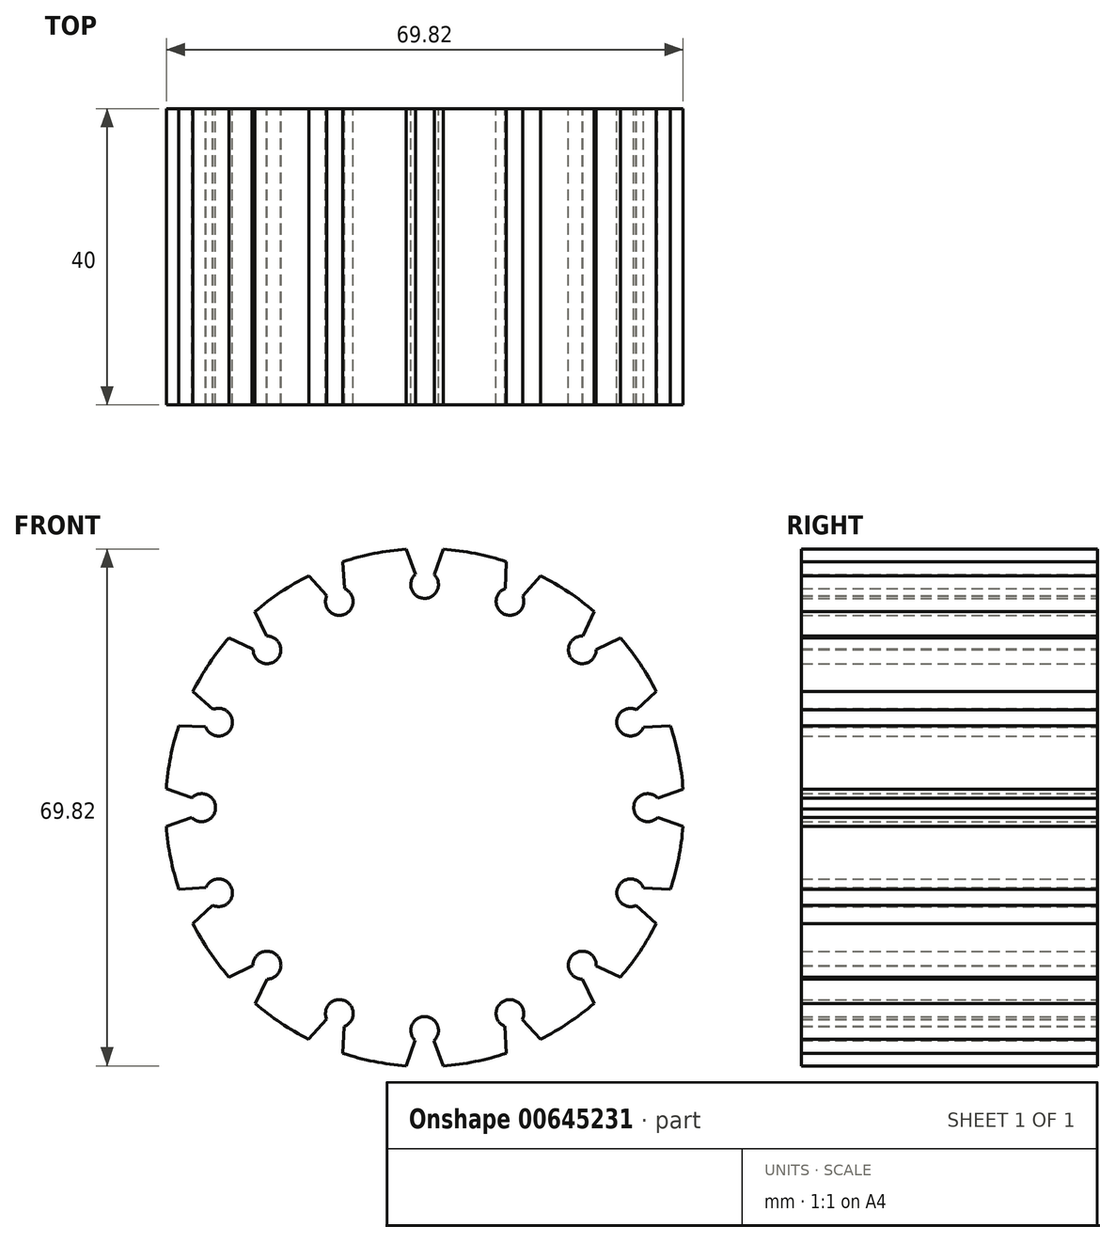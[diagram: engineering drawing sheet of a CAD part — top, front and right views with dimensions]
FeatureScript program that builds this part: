
annotation { "Feature Type Name" : "Feature", "Feature Type Description" : "" }
export const myFeature = defineFeature(function(context is Context, id is Id, definition is map)
    precondition{}
    {
        {
            var Q0;
            Q0=qCreatedBy(makeId("Front.planeOp"),FACE);
            var sketch = newSketch(context, id + "F0", { "sketchPlane" : qUnion([Q0])});
            skCircle(sketch, "E0", {"center": v(0, 0) * mm, "radius": 35 * mm});
            skLineSegment(sketch, "E1", {"start": v(0, -35) * mm, "end": v(0, 35) * mm, "construction": true});
            skLineSegment(sketch, "E2", {"start": v(35, 0) * mm, "end": v(-35, 0) * mm, "construction": true});
            skLineSegment(sketch, "E3", {"start": v(-24.75, -24.75) * mm, "end": v(24.75, 24.75) * mm, "construction": true});
            skLineSegment(sketch, "E4", {"start": v(-24.75, 24.75) * mm, "end": v(24.75, -24.75) * mm, "construction": true});
            skLineSegment(sketch, "E5.0", {"start": v(-2.5, 34.91) * mm, "end": v(2.5, 34.91) * mm});
            skLineSegment(sketch, "E6", {"start": v(-2.5, 34.91) * mm, "end": v(-1.26, 31.5) * mm});
            skLineSegment(sketch, "E7", {"start": v(2.5, 34.91) * mm, "end": v(1.3, 31.46) * mm});
            skLineSegment(sketch, "E8", {"start": v(-0.78, 30.21) * mm, "end": v(0.87, 30.21) * mm, "construction": true});
            skArc(sketch, "E9", {"start": v(-1.26, 31.5) * mm, "mid": v(-0.03, 28.25) * mm, "end": v(1.3, 31.46) * mm});
            skLineSegment(sketch, "E10", {"start": v(23.09, 26.3) * mm, "end": v(21.4, 23.13) * mm});
            skLineSegment(sketch, "E11", {"start": v(26.42, 22.96) * mm, "end": v(23.13, 21.37) * mm});
            skLineSegment(sketch, "E12", {"start": v(20.77, 21.96) * mm, "end": v(21.94, 20.8) * mm, "construction": true});
            skArc(sketch, "E13", {"start": v(21.4, 23.13) * mm, "mid": v(20, 20.02) * mm, "end": v(23.13, 21.37) * mm});
            skLineSegment(sketch, "E14", {"start": v(34.91, 2.44) * mm, "end": v(31.51, 1.2) * mm});
            skLineSegment(sketch, "E15", {"start": v(34.9, -2.55) * mm, "end": v(31.47, -1.35) * mm});
            skLineSegment(sketch, "E16", {"start": v(30.22, 0.73) * mm, "end": v(30.22, -0.92) * mm, "construction": true});
            skArc(sketch, "E17", {"start": v(31.51, 1.2) * mm, "mid": v(28.26, -0.02) * mm, "end": v(31.47, -1.35) * mm});
            skLineSegment(sketch, "E18", {"start": v(2.5, -34.91) * mm, "end": v(1.26, -31.5) * mm});
            skLineSegment(sketch, "E19", {"start": v(-2.5, -34.91) * mm, "end": v(-1.3, -31.46) * mm});
            skLineSegment(sketch, "E20", {"start": v(0.78, -30.21) * mm, "end": v(-0.87, -30.21) * mm, "construction": true});
            skArc(sketch, "E21", {"start": v(1.26, -31.5) * mm, "mid": v(0.03, -28.26) * mm, "end": v(-1.3, -31.46) * mm});
            skLineSegment(sketch, "E22", {"start": v(26.43, -22.94) * mm, "end": v(23.18, -21.4) * mm});
            skLineSegment(sketch, "E23", {"start": v(22.9, -26.48) * mm, "end": v(21.3, -23.19) * mm});
            skArc(sketch, "E24", {"start": v(23.18, -21.4) * mm, "mid": v(20, -19.94) * mm, "end": v(21.3, -23.19) * mm});
            skLineSegment(sketch, "E25.MirrorCS", {"start": v(-34.9, -2.55) * mm, "end": v(-31.47, -1.35) * mm});
            skArc(sketch, "E26.MirrorCS", {"start": v(-31.51, 1.2) * mm, "mid": v(-28.26, -0.02) * mm, "end": v(-31.47, -1.35) * mm});
            skLineSegment(sketch, "E27.MirrorCS", {"start": v(-34.91, 2.44) * mm, "end": v(-31.51, 1.2) * mm});
            skLineSegment(sketch, "E28.MirrorCS", {"start": v(-26.42, 22.96) * mm, "end": v(-23.13, 21.37) * mm});
            skArc(sketch, "E29.MirrorCS", {"start": v(-21.4, 23.13) * mm, "mid": v(-20, 20.02) * mm, "end": v(-23.13, 21.37) * mm});
            skLineSegment(sketch, "E30.MirrorCS", {"start": v(-23.09, 26.3) * mm, "end": v(-21.4, 23.13) * mm});
            skArc(sketch, "E31.MirrorCS", {"start": v(-23.18, -21.4) * mm, "mid": v(-20, -19.94) * mm, "end": v(-21.3, -23.19) * mm});
            skLineSegment(sketch, "E32.MirrorCS", {"start": v(-26.43, -22.94) * mm, "end": v(-23.18, -21.4) * mm});
            skLineSegment(sketch, "E33.MirrorCS", {"start": v(-22.9, -26.48) * mm, "end": v(-21.3, -23.19) * mm});
            skLineSegment(sketch, "E34.1.1", {"start": v(13.4, -32.34) * mm, "end": v(-13.4, 32.34) * mm, "construction": true});
            skLineSegment(sketch, "E34.1.2", {"start": v(-11.04, 33.21) * mm, "end": v(-10.84, 29.57) * mm});
            skArc(sketch, "E34.1.3", {"start": v(-13.22, 28.63) * mm, "mid": v(-10.84, 26.1) * mm, "end": v(-10.84, 29.57) * mm});
            skLineSegment(sketch, "E34.1.4", {"start": v(-15.66, 31.3) * mm, "end": v(-11.04, 33.21) * mm});
            skLineSegment(sketch, "E34.1.5", {"start": v(-15.66, 31.3) * mm, "end": v(-13.22, 28.63) * mm});
            skLineSegment(sketch, "E34.1.6", {"start": v(-12.29, 27.61) * mm, "end": v(-10.76, 28.24) * mm, "construction": true});
            skLineSegment(sketch, "E34.2.1", {"start": v(24.75, -24.75) * mm, "end": v(-24.75, 24.75) * mm, "construction": true});
            skLineSegment(sketch, "E34.2.2", {"start": v(-22.91, 26.46) * mm, "end": v(-21.33, 23.17) * mm});
            skArc(sketch, "E34.2.3", {"start": v(-23.17, 21.4) * mm, "mid": v(-20, 19.96) * mm, "end": v(-21.33, 23.17) * mm});
            skLineSegment(sketch, "E34.2.4", {"start": v(-26.45, 22.92) * mm, "end": v(-22.91, 26.46) * mm});
            skLineSegment(sketch, "E34.2.5", {"start": v(-26.45, 22.92) * mm, "end": v(-23.17, 21.4) * mm});
            skLineSegment(sketch, "E34.2.6", {"start": v(-21.92, 20.8) * mm, "end": v(-20.75, 21.98) * mm, "construction": true});
            skLineSegment(sketch, "E35.2.3.0", {"start": v(32.34, -13.4) * mm, "end": v(-32.34, 13.4) * mm, "construction": true});
            skLineSegment(sketch, "E35.5.3.0", {"start": v(-31.3, 15.68) * mm, "end": v(-28.57, 13.24) * mm});
            skArc(sketch, "E35.8.3.0", {"start": v(-29.59, 10.9) * mm, "mid": v(-26.12, 10.78) * mm, "end": v(-28.57, 13.24) * mm});
            skLineSegment(sketch, "E35.12.3.0", {"start": v(-33.2, 11.06) * mm, "end": v(-31.3, 15.68) * mm});
            skLineSegment(sketch, "E35.15.3.0", {"start": v(-33.2, 11.06) * mm, "end": v(-29.59, 10.9) * mm});
            skLineSegment(sketch, "E35.18.3.0", {"start": v(-28.21, 10.84) * mm, "end": v(-27.58, 12.36) * mm, "construction": true});
            skLineSegment(sketch, "E35.5.4.0", {"start": v(-34.91, 2.5) * mm, "end": v(-31.46, 1.3) * mm});
            skArc(sketch, "E35.8.4.0", {"start": v(-31.5, -1.26) * mm, "mid": v(-28.25, -0.03) * mm, "end": v(-31.46, 1.3) * mm});
            skLineSegment(sketch, "E35.12.4.0", {"start": v(-34.91, -2.5) * mm, "end": v(-34.91, 2.5) * mm});
            skLineSegment(sketch, "E35.15.4.0", {"start": v(-34.91, -2.5) * mm, "end": v(-31.5, -1.26) * mm});
            skLineSegment(sketch, "E35.18.4.0", {"start": v(-30.21, -0.78) * mm, "end": v(-30.21, 0.87) * mm, "construction": true});
            skLineSegment(sketch, "E35.2.5.0", {"start": v(32.34, 13.4) * mm, "end": v(-32.34, -13.4) * mm, "construction": true});
            skLineSegment(sketch, "E35.5.5.0", {"start": v(-33.21, -11.04) * mm, "end": v(-29.57, -10.84) * mm});
            skArc(sketch, "E35.8.5.0", {"start": v(-28.63, -13.22) * mm, "mid": v(-26.1, -10.84) * mm, "end": v(-29.57, -10.84) * mm});
            skLineSegment(sketch, "E35.12.5.0", {"start": v(-31.3, -15.66) * mm, "end": v(-33.21, -11.04) * mm});
            skLineSegment(sketch, "E35.15.5.0", {"start": v(-31.3, -15.66) * mm, "end": v(-28.63, -13.22) * mm});
            skLineSegment(sketch, "E35.18.5.0", {"start": v(-27.61, -12.29) * mm, "end": v(-28.24, -10.76) * mm, "construction": true});
            skLineSegment(sketch, "E35.2.6.0", {"start": v(24.75, 24.75) * mm, "end": v(-24.75, -24.75) * mm, "construction": true});
            skLineSegment(sketch, "E35.5.6.0", {"start": v(-26.46, -22.91) * mm, "end": v(-23.17, -21.33) * mm});
            skArc(sketch, "E35.8.6.0", {"start": v(-21.4, -23.17) * mm, "mid": v(-19.96, -20) * mm, "end": v(-23.17, -21.33) * mm});
            skLineSegment(sketch, "E35.12.6.0", {"start": v(-22.92, -26.45) * mm, "end": v(-26.46, -22.91) * mm});
            skLineSegment(sketch, "E35.15.6.0", {"start": v(-22.92, -26.45) * mm, "end": v(-21.4, -23.17) * mm});
            skLineSegment(sketch, "E35.18.6.0", {"start": v(-20.8, -21.92) * mm, "end": v(-21.98, -20.75) * mm, "construction": true});
            skLineSegment(sketch, "E35.2.7.0", {"start": v(13.4, 32.34) * mm, "end": v(-13.4, -32.34) * mm, "construction": true});
            skLineSegment(sketch, "E35.5.7.0", {"start": v(-15.68, -31.3) * mm, "end": v(-13.24, -28.57) * mm});
            skArc(sketch, "E35.8.7.0", {"start": v(-10.9, -29.59) * mm, "mid": v(-10.78, -26.12) * mm, "end": v(-13.24, -28.57) * mm});
            skLineSegment(sketch, "E35.12.7.0", {"start": v(-11.06, -33.2) * mm, "end": v(-15.68, -31.3) * mm});
            skLineSegment(sketch, "E35.15.7.0", {"start": v(-11.06, -33.2) * mm, "end": v(-10.9, -29.59) * mm});
            skLineSegment(sketch, "E35.18.7.0", {"start": v(-10.84, -28.21) * mm, "end": v(-12.36, -27.58) * mm, "construction": true});
            skLineSegment(sketch, "E36.2.8.0", {"start": v(0, 35) * mm, "end": v(0, -35) * mm, "construction": true});
            skArc(sketch, "E36.8.8.0", {"start": v(1.26, -31.5) * mm, "mid": v(0.03, -28.25) * mm, "end": v(-1.3, -31.46) * mm});
            skLineSegment(sketch, "E36.12.8.0", {"start": v(2.5, -34.91) * mm, "end": v(-2.5, -34.91) * mm});
            skLineSegment(sketch, "E36.2.9.0", {"start": v(-13.4, 32.34) * mm, "end": v(13.4, -32.34) * mm, "construction": true});
            skLineSegment(sketch, "E36.5.9.0", {"start": v(11.04, -33.21) * mm, "end": v(10.84, -29.57) * mm});
            skArc(sketch, "E36.8.9.0", {"start": v(13.22, -28.63) * mm, "mid": v(10.84, -26.1) * mm, "end": v(10.84, -29.57) * mm});
            skLineSegment(sketch, "E36.12.9.0", {"start": v(15.66, -31.3) * mm, "end": v(11.04, -33.21) * mm});
            skLineSegment(sketch, "E36.15.9.0", {"start": v(15.66, -31.3) * mm, "end": v(13.22, -28.63) * mm});
            skLineSegment(sketch, "E36.18.9.0", {"start": v(12.29, -27.61) * mm, "end": v(10.76, -28.24) * mm, "construction": true});
            skLineSegment(sketch, "E36.5.10.0", {"start": v(22.91, -26.46) * mm, "end": v(21.33, -23.17) * mm});
            skArc(sketch, "E36.8.10.0", {"start": v(23.17, -21.4) * mm, "mid": v(20, -19.96) * mm, "end": v(21.33, -23.17) * mm});
            skLineSegment(sketch, "E36.12.10.0", {"start": v(26.45, -22.92) * mm, "end": v(22.91, -26.46) * mm});
            skLineSegment(sketch, "E36.15.10.0", {"start": v(26.45, -22.92) * mm, "end": v(23.17, -21.4) * mm});
            skLineSegment(sketch, "E36.18.10.0", {"start": v(21.92, -20.8) * mm, "end": v(20.75, -21.98) * mm, "construction": true});
            skLineSegment(sketch, "E36.2.11.0", {"start": v(-32.34, 13.4) * mm, "end": v(32.34, -13.4) * mm, "construction": true});
            skLineSegment(sketch, "E36.5.11.0", {"start": v(31.3, -15.68) * mm, "end": v(28.57, -13.24) * mm});
            skArc(sketch, "E36.8.11.0", {"start": v(29.59, -10.9) * mm, "mid": v(26.12, -10.78) * mm, "end": v(28.57, -13.24) * mm});
            skLineSegment(sketch, "E36.12.11.0", {"start": v(33.2, -11.06) * mm, "end": v(31.3, -15.68) * mm});
            skLineSegment(sketch, "E36.15.11.0", {"start": v(33.2, -11.06) * mm, "end": v(29.59, -10.9) * mm});
            skLineSegment(sketch, "E36.18.11.0", {"start": v(28.21, -10.84) * mm, "end": v(27.58, -12.36) * mm, "construction": true});
            skLineSegment(sketch, "E37.2.12.0", {"start": v(-35, 0) * mm, "end": v(35, 0) * mm, "construction": true});
            skLineSegment(sketch, "E37.5.12.0", {"start": v(34.91, -2.5) * mm, "end": v(31.46, -1.3) * mm});
            skArc(sketch, "E37.8.12.0", {"start": v(31.5, 1.26) * mm, "mid": v(28.25, 0.03) * mm, "end": v(31.46, -1.3) * mm});
            skLineSegment(sketch, "E37.12.12.0", {"start": v(34.91, 2.5) * mm, "end": v(34.91, -2.5) * mm});
            skLineSegment(sketch, "E37.15.12.0", {"start": v(34.91, 2.5) * mm, "end": v(31.5, 1.26) * mm});
            skLineSegment(sketch, "E37.18.12.0", {"start": v(30.21, 0.78) * mm, "end": v(30.21, -0.87) * mm, "construction": true});
            skLineSegment(sketch, "E37.2.13.0", {"start": v(-32.34, -13.4) * mm, "end": v(32.34, 13.4) * mm, "construction": true});
            skLineSegment(sketch, "E37.5.13.0", {"start": v(33.21, 11.04) * mm, "end": v(29.57, 10.84) * mm});
            skArc(sketch, "E37.8.13.0", {"start": v(28.63, 13.22) * mm, "mid": v(26.1, 10.84) * mm, "end": v(29.57, 10.84) * mm});
            skLineSegment(sketch, "E37.12.13.0", {"start": v(31.3, 15.66) * mm, "end": v(33.21, 11.04) * mm});
            skLineSegment(sketch, "E37.15.13.0", {"start": v(31.3, 15.66) * mm, "end": v(28.63, 13.22) * mm});
            skLineSegment(sketch, "E37.18.13.0", {"start": v(27.61, 12.29) * mm, "end": v(28.24, 10.76) * mm, "construction": true});
            skLineSegment(sketch, "E38.5.14.0", {"start": v(26.46, 22.91) * mm, "end": v(23.17, 21.33) * mm});
            skArc(sketch, "E38.8.14.0", {"start": v(21.4, 23.17) * mm, "mid": v(19.96, 20) * mm, "end": v(23.17, 21.33) * mm});
            skLineSegment(sketch, "E38.12.14.0", {"start": v(22.92, 26.45) * mm, "end": v(26.46, 22.91) * mm});
            skLineSegment(sketch, "E38.15.14.0", {"start": v(22.92, 26.45) * mm, "end": v(21.4, 23.17) * mm});
            skLineSegment(sketch, "E38.18.14.0", {"start": v(20.8, 21.92) * mm, "end": v(21.98, 20.75) * mm, "construction": true});
            skLineSegment(sketch, "E38.2.15.0", {"start": v(-13.4, -32.34) * mm, "end": v(13.4, 32.34) * mm, "construction": true});
            skLineSegment(sketch, "E38.5.15.0", {"start": v(15.68, 31.3) * mm, "end": v(13.24, 28.57) * mm});
            skArc(sketch, "E38.8.15.0", {"start": v(10.9, 29.59) * mm, "mid": v(10.78, 26.12) * mm, "end": v(13.24, 28.57) * mm});
            skLineSegment(sketch, "E38.12.15.0", {"start": v(11.06, 33.2) * mm, "end": v(15.68, 31.3) * mm});
            skLineSegment(sketch, "E38.15.15.0", {"start": v(11.06, 33.2) * mm, "end": v(10.9, 29.59) * mm});
            skLineSegment(sketch, "E38.18.15.0", {"start": v(10.84, 28.21) * mm, "end": v(12.36, 27.58) * mm, "construction": true});
            skSolve(sketch);
        }
        {
            var Q0;
            {var subQ1=sQuery(id+"F0.wireOp",EDGE,"E7");Q0=makeQuery(id+"F0.imprint","IMPRINT",FACE,{"disambiguationData":[TD([[makeQuery(id+"F0.imprint","IMPRINT",EDGE,{"derivedFrom":subQ1}),1.0]])]});}
            extrude(context, id + "F1", {"entities" : qUnion([Q0]), "endBound" : BoundingType.SYMMETRIC, "depth" : 40 * mm, "offsetDistance" : 25 * mm});
        }
    });
